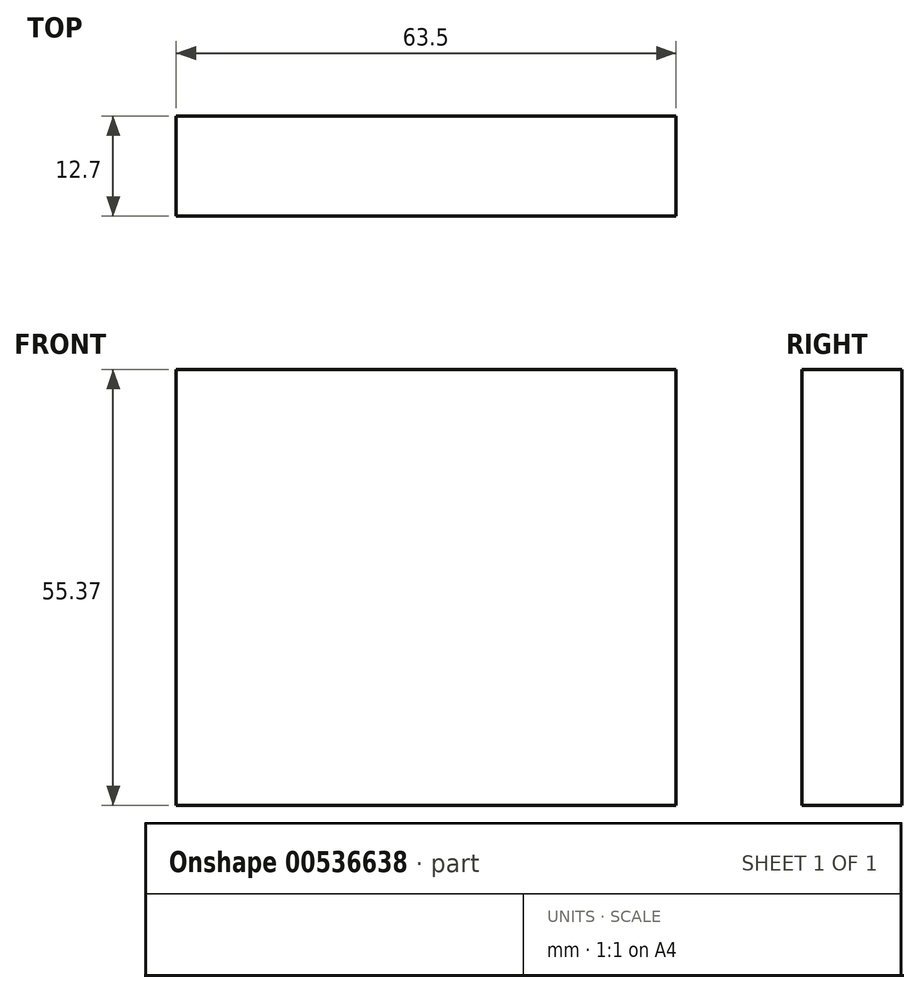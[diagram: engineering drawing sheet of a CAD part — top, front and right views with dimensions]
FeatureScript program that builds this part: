
annotation { "Feature Type Name" : "Feature", "Feature Type Description" : "" }
export const myFeature = defineFeature(function(context is Context, id is Id, definition is map)
    precondition{}
    {
        {
            var Q0;
            Q0=qCreatedBy(makeId("Front.planeOp"),FACE);
            var sketch = newSketch(context, id + "F0", { "sketchPlane" : qUnion([Q0])});
            skLineSegment(sketch, "E0.bottom", {"start": v(-33.5, 34.26) * mm, "end": v(30, 34.26) * mm});
            skLineSegment(sketch, "E0.top", {"start": v(-33.5, -21.11) * mm, "end": v(30, -21.11) * mm});
            skLineSegment(sketch, "E0.left", {"start": v(-33.5, 34.26) * mm, "end": v(-33.5, -21.11) * mm});
            skLineSegment(sketch, "E0.right", {"start": v(30, 34.26) * mm, "end": v(30, -21.11) * mm});
            skSolve(sketch);
        }
        {
            var Q0;
            Q0 = qSketchRegion(id + "F0", true);
            extrude(context, id + "F1", {"entities" : qUnion([Q0]), "depth" : 12.7 * mm, "offsetDistance" : 25.4 * mm});
        }
    });
